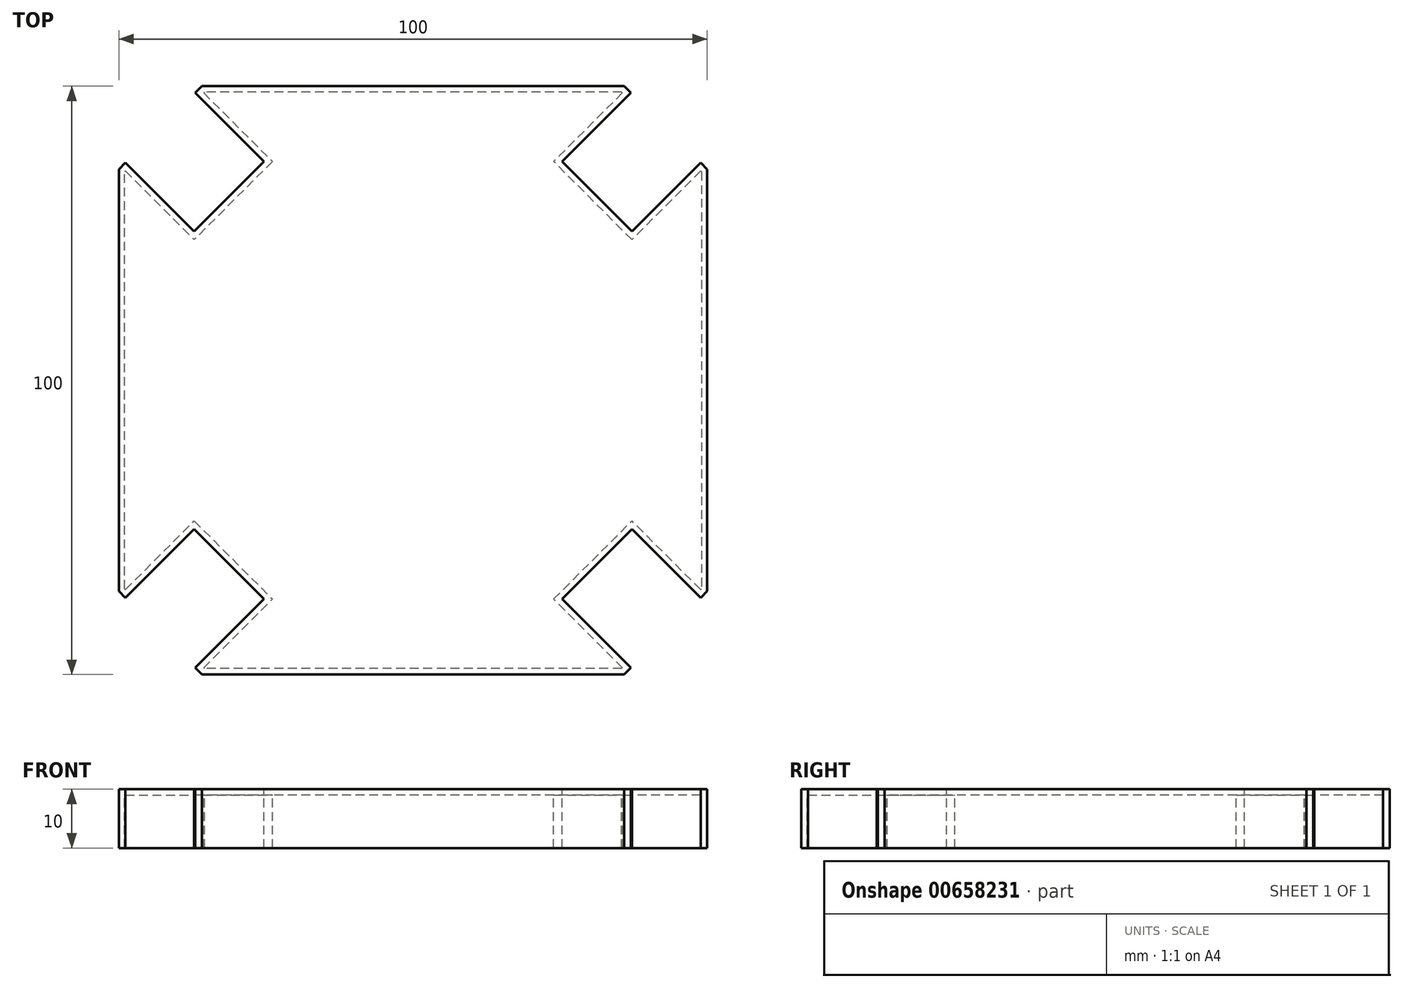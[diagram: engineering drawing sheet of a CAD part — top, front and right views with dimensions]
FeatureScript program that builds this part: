
annotation { "Feature Type Name" : "Feature", "Feature Type Description" : "" }
export const myFeature = defineFeature(function(context is Context, id is Id, definition is map)
    precondition{}
    {
        {
            var Q0;
            Q0=qCreatedBy(makeId("Top.planeOp"),FACE);
            var sketch = newSketch(context, id + "F0", { "sketchPlane" : qUnion([Q0])});
            skLineSegment(sketch, "E0.top", {"start": v(35.86, 50) * mm, "end": v(-35.86, 50) * mm});
            skLineSegment(sketch, "E0.right", {"start": v(-50, -35.86) * mm, "end": v(-50, 35.86) * mm});
            skPoint(sketch, "E0.middle", {"position": v(0, 0) * mm});
            skLineSegment(sketch, "E1", {"start": v(50, 35.86) * mm, "end": v(50, -35.86) * mm});
            skLineSegment(sketch, "E2", {"start": v(35.86, -50) * mm, "end": v(-35.86, -50) * mm});
            skPoint(sketch, "E3.orphan", {"position": v(50, -50) * mm});
            skPoint(sketch, "E4.orphan", {"position": v(50, 50) * mm});
            skPoint(sketch, "E5.orphan", {"position": v(-50, 50) * mm});
            skPoint(sketch, "E6.orphan", {"position": v(-50, -50) * mm});
            skLineSegment(sketch, "E7.0", {"start": v(-48.87, -36.99) * mm, "end": v(-37.2, -25.31) * mm});
            skLineSegment(sketch, "E8.0", {"start": v(-36.99, -48.87) * mm, "end": v(-25.31, -37.2) * mm});
            skLineSegment(sketch, "E9", {"start": v(-48.87, -36.99) * mm, "end": v(-50, -35.86) * mm});
            skLineSegment(sketch, "E10", {"start": v(-36.99, -48.87) * mm, "end": v(-35.86, -50) * mm});
            skLineSegment(sketch, "E11.0", {"start": v(-37.2, -25.31) * mm, "end": v(-25.31, -37.2) * mm});
            skLineSegment(sketch, "E12.1.0", {"start": v(36.99, -48.87) * mm, "end": v(35.86, -50) * mm});
            skLineSegment(sketch, "E12.1.2", {"start": v(36.99, -48.87) * mm, "end": v(25.31, -37.2) * mm});
            skLineSegment(sketch, "E12.1.3", {"start": v(48.87, -36.99) * mm, "end": v(50, -35.86) * mm});
            skLineSegment(sketch, "E12.1.4", {"start": v(48.87, -36.99) * mm, "end": v(37.2, -25.31) * mm});
            skLineSegment(sketch, "E12.1.6", {"start": v(25.31, -37.2) * mm, "end": v(37.2, -25.31) * mm});
            skLineSegment(sketch, "E12.2.0", {"start": v(48.87, 36.99) * mm, "end": v(50, 35.86) * mm});
            skLineSegment(sketch, "E12.2.2", {"start": v(48.87, 36.99) * mm, "end": v(37.2, 25.31) * mm});
            skLineSegment(sketch, "E12.2.3", {"start": v(36.99, 48.87) * mm, "end": v(35.86, 50) * mm});
            skLineSegment(sketch, "E12.2.4", {"start": v(36.99, 48.87) * mm, "end": v(25.31, 37.2) * mm});
            skLineSegment(sketch, "E12.2.6", {"start": v(37.2, 25.31) * mm, "end": v(25.31, 37.2) * mm});
            skLineSegment(sketch, "E12.3.0", {"start": v(-36.99, 48.87) * mm, "end": v(-35.86, 50) * mm});
            skLineSegment(sketch, "E12.3.2", {"start": v(-36.99, 48.87) * mm, "end": v(-25.31, 37.2) * mm});
            skLineSegment(sketch, "E12.3.3", {"start": v(-48.87, 36.99) * mm, "end": v(-50, 35.86) * mm});
            skLineSegment(sketch, "E12.3.4", {"start": v(-48.87, 36.99) * mm, "end": v(-37.2, 25.31) * mm});
            skLineSegment(sketch, "E12.3.6", {"start": v(-25.31, 37.2) * mm, "end": v(-37.2, 25.31) * mm});
            skSolve(sketch);
        }
        {
            var Q0;
            Q0=makeQuery(id+"F0.imprint","IMPRINT",FACE,{"disambiguationData":[TD([[makeQuery(id+"F0.imprint","IMPRINT",EDGE,{"derivedFrom":sQuery(id+"F0.wireOp",EDGE,"E0.top")}),1.0]])]});
            extrude(context, id + "F1", {"entities" : qUnion([Q0]), "oppositeDirection" : true, "depth" : 10 * mm, "offsetDistance" : 25 * mm});
        }
        {
            var Q0;
            Q0=makeQuery(id+"F1.opExtrude","CAP_FACE",FACE,{"disambiguationData":[OSD([sQuery(id+"F0.wireOp",EDGE,"E0.top"),sQuery(id+"F0.wireOp",EDGE,"E0.right"),sQuery(id+"F0.wireOp",EDGE,"E1"),sQuery(id+"F0.wireOp",EDGE,"E2"),sQuery(id+"F0.wireOp",EDGE,"E7.0"),sQuery(id+"F0.wireOp",EDGE,"E8.0"),sQuery(id+"F0.wireOp",EDGE,"E9"),sQuery(id+"F0.wireOp",EDGE,"E10"),sQuery(id+"F0.wireOp",EDGE,"E11.0"),sQuery(id+"F0.wireOp",EDGE,"E12.1.0"),sQuery(id+"F0.wireOp",EDGE,"E12.1.2"),sQuery(id+"F0.wireOp",EDGE,"E12.1.3"),sQuery(id+"F0.wireOp",EDGE,"E12.1.4"),sQuery(id+"F0.wireOp",EDGE,"E12.1.6"),sQuery(id+"F0.wireOp",EDGE,"E12.2.0"),sQuery(id+"F0.wireOp",EDGE,"E12.2.2"),sQuery(id+"F0.wireOp",EDGE,"E12.2.3"),sQuery(id+"F0.wireOp",EDGE,"E12.2.4"),sQuery(id+"F0.wireOp",EDGE,"E12.2.6"),sQuery(id+"F0.wireOp",EDGE,"E12.3.0"),sQuery(id+"F0.wireOp",EDGE,"E12.3.2"),sQuery(id+"F0.wireOp",EDGE,"E12.3.3"),sQuery(id+"F0.wireOp",EDGE,"E12.3.4"),sQuery(id+"F0.wireOp",EDGE,"E12.3.6")])],"isStart":false});
            shell(context, id + "F2", {"entities" : qUnion([Q0]), "thickness" : 1 * mm});
        }
    });
